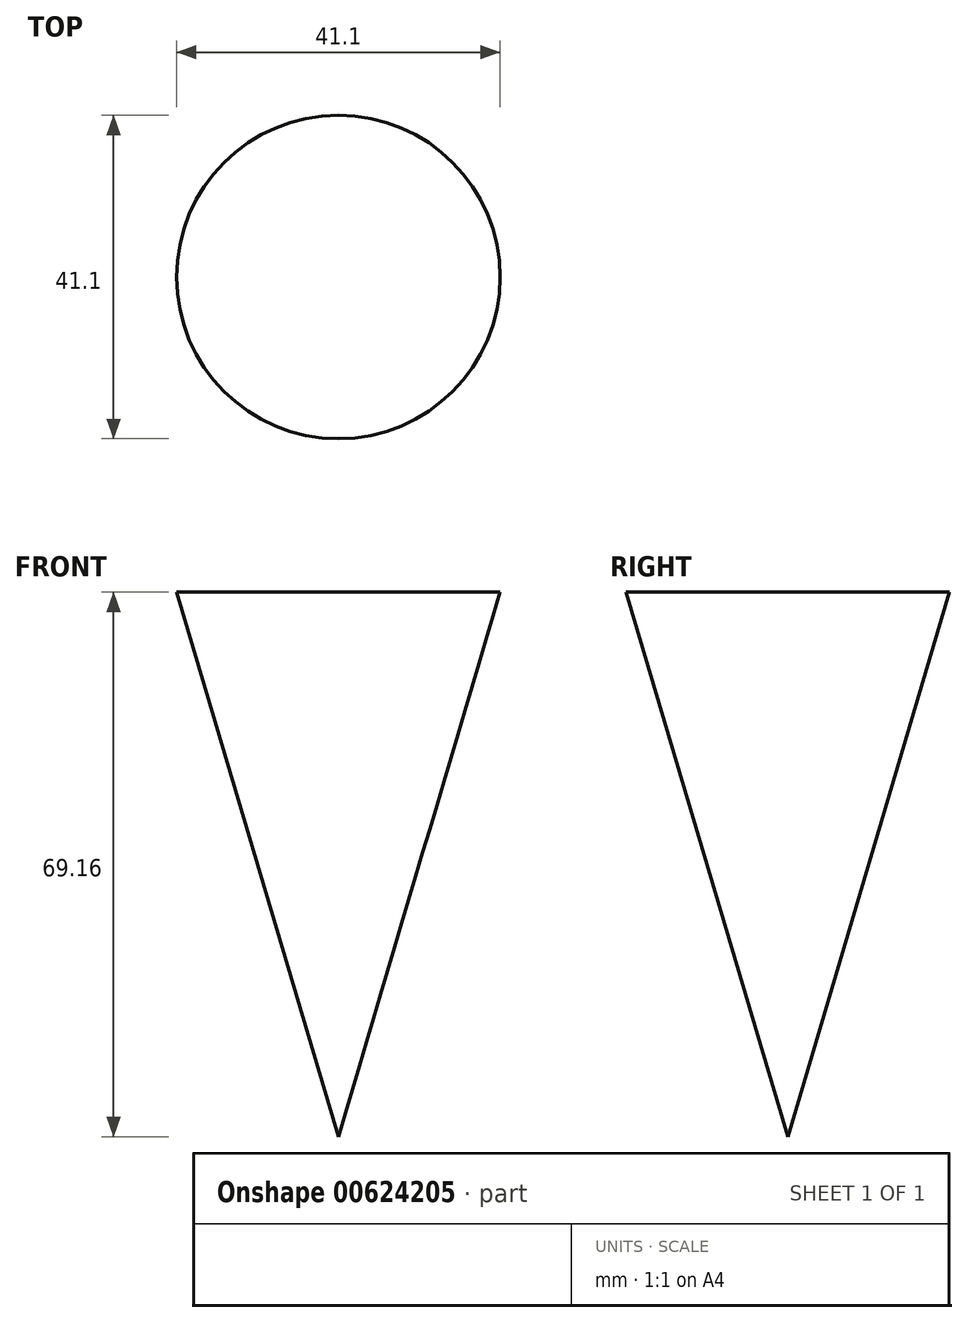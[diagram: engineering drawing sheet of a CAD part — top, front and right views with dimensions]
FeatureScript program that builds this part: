
annotation { "Feature Type Name" : "Feature", "Feature Type Description" : "" }
export const myFeature = defineFeature(function(context is Context, id is Id, definition is map)
    precondition{}
    {
        {
            var Q0;
            Q0=qCreatedBy(makeId("Front.planeOp"),FACE);
            var sketch = newSketch(context, id + "F0", { "sketchPlane" : qUnion([Q0])});
            skLineSegment(sketch, "E0", {"start": v(-20.55, 69.16) * mm, "end": v(0, 69.16) * mm});
            skLineSegment(sketch, "E1", {"start": v(0, 69.16) * mm, "end": v(0, 0) * mm});
            skLineSegment(sketch, "E2", {"start": v(0, 0) * mm, "end": v(-20.55, 69.16) * mm});
            skSolve(sketch);
        }
        {
            var Q0;
            Q0=makeQuery(id+"F0.imprint","IMPRINT",FACE,{"disambiguationData":[TD([[makeQuery(id+"F0.imprint","IMPRINT",EDGE,{"derivedFrom":sQuery(id+"F0.wireOp",EDGE,"E0")}),-1.0]])]});
            var Q1;
            Q1=sQuery(id+"F0.wireOp",EDGE,"E1");
            revolve(context, id + "F1", {"entities" : qUnion([Q0]), "axis" : qUnion([Q1]), "revolveType" : RevolveType.FULL});
        }
    });
